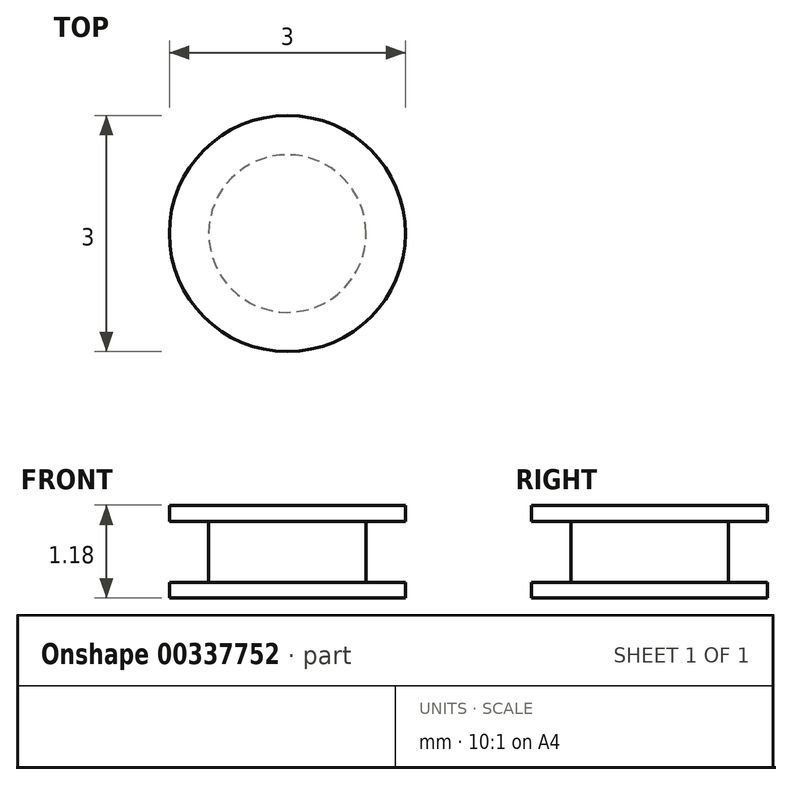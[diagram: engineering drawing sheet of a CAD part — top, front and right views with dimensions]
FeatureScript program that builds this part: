
annotation { "Feature Type Name" : "Feature", "Feature Type Description" : "" }
export const myFeature = defineFeature(function(context is Context, id is Id, definition is map)
    precondition{}
    {
        {
            var Q0;
            Q0=qCreatedBy(makeId("Top.planeOp"),FACE);
            var sketch = newSketch(context, id + "F0", { "sketchPlane" : qUnion([Q0])});
            skCircle(sketch, "E0", {"center": v(0, 0) * mm, "radius": 1 * mm});
            skSolve(sketch);
        }
        {
            var Q0;
            Q0 = qSketchRegion(id + "F0", true);
            extrude(context, id + "F1", {"entities" : qUnion([Q0]), "depth" : (.388 * 2) * mm});
        }
        {
            var Q0;
            Q0=makeQuery(id+"F1.opExtrude","CAP_FACE",FACE,{"disambiguationData":[OSD([sQuery(id+"F0.wireOp",EDGE,"E0")])],"isStart":false});
            var sketch = newSketch(context, id + "F2", { "sketchPlane" : qUnion([Q0])});
            skCircle(sketch, "E1", {"center": v(0, 0) * mm, "radius": 1.5 * mm});
            skSolve(sketch);
        }
        {
            var Q0;
            Q0=makeQuery(id+"F2.imprint","IMPRINT",FACE,{"disambiguationData":[TD([[makeQuery(id+"F2.imprint","IMPRINT",EDGE,{"derivedFrom":sQuery(id+"F2.wireOp",EDGE,"E1")}),1.0]])]});
            var Q1;
            Q1=makeQuery(id+"F2.imprint","IMPRINT",FACE,{"disambiguationData":[TD([[makeQuery(id+"F2.imprint","IMPRINT",EDGE,{"derivedFrom":makeQuery(id+"F1.opExtrude","CAP_EDGE",EDGE,{"disambiguationData":[OSD([sQuery(id+"F0.wireOp",EDGE,"E0")])],"isStart":false})}),1.0]])]});
            extrude(context, id + "F3", {"entities" : qUnion([Q0, Q1]), "operationType" : NewBodyOperationType.ADD, "depth" : .2 * mm});
        }
        {
            var Q0;
            Q0=makeQuery(id+"F1.opExtrude","CAP_FACE",FACE,{"disambiguationData":[OSD([sQuery(id+"F0.wireOp",EDGE,"E0")])],"isStart":true});
            var sketch = newSketch(context, id + "F4", { "sketchPlane" : qUnion([Q0])});
            skCircle(sketch, "E2", {"center": v(0, 0) * mm, "radius": 1.5 * mm});
            skSolve(sketch);
        }
        {
            var Q0;
            Q0=makeQuery(id+"F4.imprint","IMPRINT",FACE,{"disambiguationData":[TD([[makeQuery(id+"F4.imprint","IMPRINT",EDGE,{"derivedFrom":makeQuery(id+"F1.opExtrude","CAP_EDGE",EDGE,{"disambiguationData":[OSD([sQuery(id+"F0.wireOp",EDGE,"E0")])],"isStart":true})}),-1.0]])]});
            var Q1;
            Q1=makeQuery(id+"F4.imprint","IMPRINT",FACE,{"disambiguationData":[TD([[makeQuery(id+"F4.imprint","IMPRINT",EDGE,{"derivedFrom":sQuery(id+"F4.wireOp",EDGE,"E2")}),1.0]])]});
            extrude(context, id + "F5", {"entities" : qUnion([Q0, Q1]), "operationType" : NewBodyOperationType.ADD, "depth" : .2 * mm});
        }
    });
